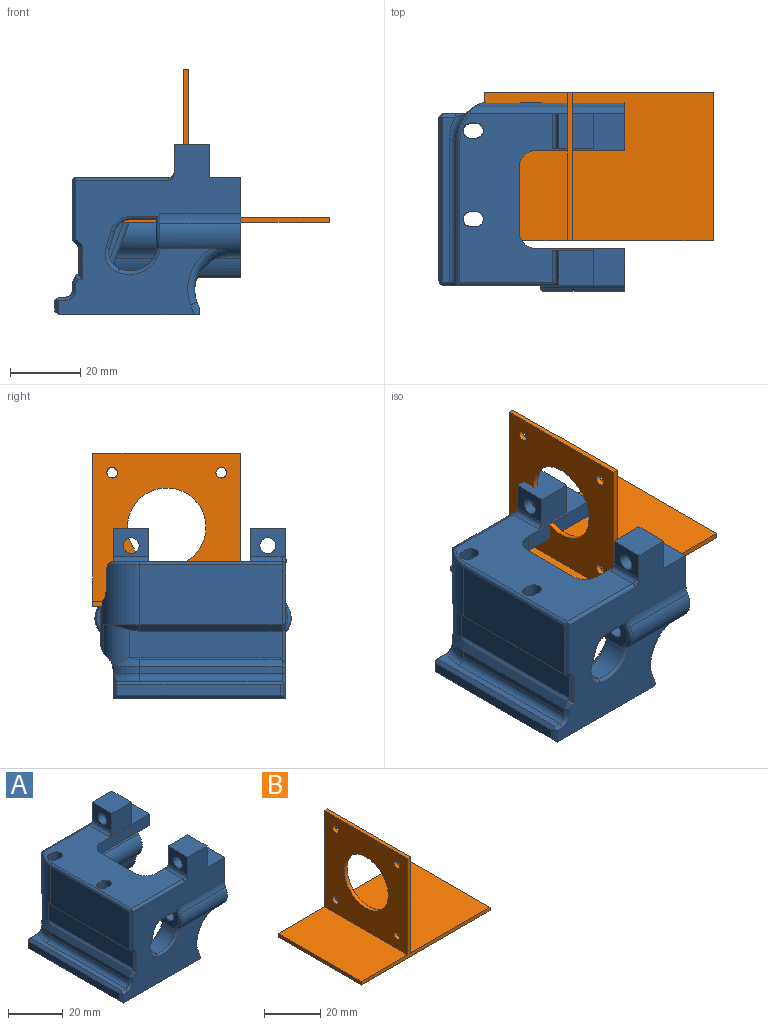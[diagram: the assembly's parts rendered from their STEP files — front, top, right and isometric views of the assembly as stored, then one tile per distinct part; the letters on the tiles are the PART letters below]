
ASSEMBLY  parts=2 mates=1
PART A: 215 faces, bbox 55x69.2x51.2 mm
  f0: cylinder r=11mm len=7.18mm, axis (0,0,-1), area 15.4mm2, adj f1,f133,f176,f195,f196
  f1: plane 40.6x2mm, normal (-1,0,0), area 81.2mm2, adj f0,f132,f175,f187
  f2: cylinder r=11mm len=25.09mm, axis (0,0,-1), area 262.1mm2, adj f47,f72,f73,f77,f80,f81,f174,f178
  f3: cylinder r=2mm len=25mm, axis (0,0,-1), area 11.6mm2, adj f7,f33,f36,f60,f137
  f4: plane 14x5.5mm, normal (1,0,0), area 77mm2, adj f5,f33,f60,f172
  f5: plane 22.15x7.04mm, normal (0.45,0,0.89), area 85.2mm2, adj f4,f7,f22,f26,f36,f60,f104,f124
  f6: plane 22.15x7.04mm, normal (0.45,0,-0.89), area 85.2mm2, adj f7,f9,f11,f22,f25,f26,f60,f126
  f7: plane 11x0.03mm, normal (-1,0,0), area 0.3mm2, adj f3,f5,f6,f149
  f8: plane 49x46.8mm, normal (0,0,1), area 1158.1mm2, adj f28,f50,f59,f60,f61,f62,f63,f64
  f9: plane 7x3.25mm, normal (1,0,0), area 22.7mm2, adj f6,f25,f34,f136
  f10: plane 7x3.25mm, normal (1,0,0), area 22.7mm2, adj f24,f49,f127,f134
  f11: plane 5x4.05mm, normal (1,0,0), area 20.2mm2, adj f6,f136,f170,f207
  f12: plane 7x0.55mm, normal (1,0,0), area 3.8mm2, adj f43,f45,f49,f127,f134
  f13: cylinder r=2mm len=2mm, axis (0,0,-1), area 6.3mm2, adj f15,f34,f52,f58
  f14: cylinder r=2mm len=2mm, axis (0,0,-1), area 6.3mm2, adj f15,f34,f51,f58
  f15: plane 2x0.2mm, normal (1,0,0), area 0.4mm2, adj f13,f14,f34,f58
  f16: cylinder r=2mm len=2mm, axis (0,0,-1), area 6.3mm2, adj f17,f49,f54,f58
  f17: plane 2x0.2mm, normal (1,0,0), area 0.4mm2, adj f16,f18,f49,f58
  f18: cylinder r=2mm len=2mm, axis (0,0,-1), area 6.3mm2, adj f17,f49,f56,f58
  f19: cylinder r=5mm len=3.66mm, axis (-1,0,0), area 7.5mm2, adj f20,f21,f71,f130,f131
  f20: cylinder r=5mm len=2.74mm, axis (-1,0,0), area 0.4mm2, adj f19,f21,f71,f131
  f21: cylinder r=9.6mm len=39.88mm, axis (1,0,0), area 186.7mm2, adj f19,f20,f66,f71,f88,f89,f129,f130
  f22: plane 27.41x10.4mm, normal (0,-1,0), area 123.5mm2, adj f5,f6,f25,f103,f104,f110,f124,f125
  f23: plane 27.41x10.4mm, normal (0,1,0), area 123.5mm2, adj f24,f101,f102,f106,f127,f128,f129,f130
  f24: cylinder r=3mm len=8.5mm, axis (0,0,1), area 36.2mm2, adj f10,f23,f49,f105,f127
  f25: cylinder r=3mm len=8.5mm, axis (0,0,-1), area 36.2mm2, adj f6,f9,f22,f34,f109
  f26: plane 41.8x31mm, normal (0,1,0), area 577.4mm2, adj f5,f6,f28,f30,f58,f124,f125,f126
  f27: plane 45.17x8.35mm, normal (0,0,-1), area 329.3mm2, adj f41,f42,f48,f55,f62,f63,f65,f66
  f28: plane 22.19x12.09mm, normal (1,0,0), area 202.2mm2, adj f8,f26,f29,f30,f50,f119,f120,f123
  f29: cylinder r=6.09mm len=23mm, axis (1,0,0), area 98.7mm2, adj f28,f120,f161,f168
  f30: cylinder r=6.09mm len=24mm, axis (1,0,0), area 314.6mm2, adj f26,f28,f31,f50,f120,f155,f160,f165
  f31: plane 10.19x9.28mm, normal (-1,0,0), area 64.3mm2, adj f30,f32,f115,f119,f156,f161,f165,f166
  f32: plane 7.11x6.5mm, normal (0,0,-1), area 46.2mm2, adj f31,f118,f156,f161
  f33: plane 17.17x14mm, normal (0,0,-1), area 191.8mm2, adj f3,f4,f36,f59,f60,f61,f67,f103
  f34: plane 19.69x6.7mm, normal (0,0,1), area 53.5mm2, adj f9,f13,f14,f15,f25,f35,f51,f52
  f35: plane 6.4x2mm, normal (1,0,0), area 12.8mm2, adj f34,f51,f58,f206
  f36: plane 14x4.67mm, normal (1,0,0), area 65.4mm2, adj f3,f5,f33,f104
  f37: plane 6.74x6.42mm, normal (0.92,0,-0.39), area 43.7mm2, adj f70,f79,f85,f86,f94,f95
  f38: plane 1x0.64mm, normal (0.92,0,-0.39), area 0.7mm2, adj f44,f45,f57,f99
  f39: cylinder r=6mm len=40.16mm, axis (1,0,0), area 408.5mm2, adj f65,f66,f75,f84,f88
  f40: cylinder r=6mm len=23.5mm, axis (1,0,0), area 201.7mm2, adj f66,f77,f90,f97
  f41: plane 6.67x1.68mm, normal (-1,0,0), area 0.5mm2, adj f27,f42,f74,f75,f84
  f42: plane 17.05x3.25mm, normal (0,-1,0), area 55.4mm2, adj f27,f41,f65,f84
  f43: cylinder r=5mm len=19.17mm, axis (-1,0,0), area 27.8mm2, adj f12,f45,f89,f99,f127
  f44: plane 15.23x7.83mm, normal (0,1,0), area 69.2mm2, adj f38,f57,f58,f82,f99,f191,f193,f194
  f45: plane 10.2x7.27mm, normal (0,-1,0), area 43mm2, adj f12,f38,f43,f49,f99
  f46: plane 5.72x4.3mm, normal (0,0,-1), area 24.6mm2, adj f70,f78,f83,f91
  f47: plane 40.6x17mm, normal (-1,0,0), area 690.2mm2, adj f2,f177,f179,f198
  f48: plane 14x4.67mm, normal (1,0,0), area 65.4mm2, adj f27,f55,f102,f128
  f49: plane 15.19x6.7mm, normal (0,0,1), area 45.6mm2, adj f10,f12,f16,f17,f18,f24,f45,f53
  f50: plane 52.4x49.1mm, normal (0,-1,0), area 1198.7mm2, adj f8,f28,f30,f58,f138,f140,f141,f155
  f51: plane 3x2mm, normal (0,1,0), area 6mm2, adj f14,f34,f35,f58
  f52: plane 3x2mm, normal (0,-1,0), area 6mm2, adj f13,f34,f53,f58
  f53: plane 20.8x2mm, normal (1,0,0), area 41.6mm2, adj f34,f49,f52,f54,f58,f100
  f54: plane 3x2mm, normal (0,1,0), area 6mm2, adj f16,f49,f53,f58
  f55: cylinder r=2mm len=25mm, axis (0,0,-1), area 11.6mm2, adj f27,f48,f63,f87,f135
  f56: plane 3x2mm, normal (0,-1,0), area 6mm2, adj f18,f49,f57,f58
  f57: plane 2.9x2mm, normal (1,0,0), area 5.8mm2, adj f38,f44,f49,f56,f58
  f58: plane 49.03x40.03mm, normal (0,0,-1), area 747.4mm2, adj f13,f14,f15,f16,f17,f18,f26,f35
  f59: plane 5x1.5mm, normal (0,1,0), area 7.5mm2, adj f8,f33,f60,f67
  f60: cylinder r=2.15mm len=30mm, axis (0,0,-1), area 150.4mm2, adj f3,f4,f5,f6,f8,f33,f59,f61
  f61: plane 5x1.5mm, normal (0,-1,0), area 7.5mm2, adj f8,f33,f60,f67
  f62: plane 5x1.5mm, normal (0,1,0), area 7.5mm2, adj f8,f27,f63,f65
  f63: cylinder r=2.15mm len=30mm, axis (0,0,-1), area 165.2mm2, adj f8,f27,f55,f62,f64,f127,f135
  f64: plane 29.5x1.5mm, normal (0,-1,0), area 43.7mm2, adj f8,f63,f65,f127
  f65: cylinder r=2.15mm len=28.75mm, axis (0,0,-1), area 128.2mm2, adj f8,f27,f39,f42,f62,f64,f79,f83
  f66: plane 28.45x15.72mm, normal (1,0,0), area 225.5mm2, adj f8,f21,f27,f39,f40,f72,f73,f74
  f67: cylinder r=2.15mm len=5mm, axis (0,0,-1), area 33.8mm2, adj f8,f33,f59,f61
  f68: plane 47x3.69mm, normal (0,0,1), area 97.5mm2, adj f132,f133,f184,f190,f193
  f69: plane 46.59x3mm, normal (-1,0,0), area 139.8mm2, adj f188,f189,f190,f191
  f70: cylinder r=2.9mm len=6.25mm, axis (0,1,0), area 20.7mm2, adj f37,f46,f79,f92,f93
  f71: plane 2.55x1.16mm, normal (0.92,0,-0.39), area 0.2mm2, adj f19,f20,f21
  f72: plane 42.51x5.47mm, normal (0,1,0), area 232.7mm2, adj f2,f66,f73,f77
  f73: cylinder r=2.5mm len=43.52mm, axis (1,0,0), area 147.7mm2, adj f2,f8,f66,f72,f142,f199
  f74: plane 24x2.98mm, normal (0,-1,0), area 71.5mm2, adj f27,f41,f66,f75
  f75: cylinder r=5mm len=24mm, axis (1,0,0), area 99.7mm2, adj f39,f41,f66,f74
  f76: cylinder r=2.25mm len=24mm, axis (1,0,0), area 339.3mm2, adj f66,f78
  f77: cylinder r=6mm len=42.51mm, axis (1,0,0), area 179.7mm2, adj f2,f40,f66,f72,f80,f91,f92,f96
  f78: plane 9.67x8.43mm, normal (-1,0,0), area 53mm2, adj f46,f76,f83,f85,f86,f91,f95,f96
  f79: plane 12.75x7.58mm, normal (0,-1,0), area 70.6mm2, adj f37,f65,f70,f83,f85
  f80: plane 36.85x11.25mm, normal (0,1,0), area 128.2mm2, adj f2,f66,f77,f81,f92,f93,f94,f95
  f81: cylinder r=5mm len=43.61mm, axis (-1,0,0), area 165.8mm2, adj f2,f66,f80,f82,f174,f196
  f82: cylinder r=6mm len=44.48mm, axis (-1,0,0), area 91.8mm2, adj f44,f66,f81,f89,f99,f196
  f83: cylinder r=5.5mm len=17.05mm, axis (1,0,0), area 28.9mm2, adj f46,f65,f78,f79,f85
  f84: cylinder r=4.32mm len=17.05mm, axis (1,0,0), area 65.5mm2, adj f39,f41,f42,f65
  f85: cylinder r=4.2mm len=17.05mm, axis (1,0,0), area 141.1mm2, adj f37,f65,f78,f79,f83,f86
  f86: plane 9.75x3.7mm, normal (0,-0.03,1), area 36mm2, adj f37,f78,f85,f95
  f87: plane 11x0.03mm, normal (-1,0,0), area 0.3mm2, adj f55,f127,f128,f153
  f88: cylinder r=3.72mm len=40.3mm, axis (1,0,0), area 104.5mm2, adj f21,f39,f65,f66,f128,f129
  f89: cylinder r=1.71mm len=40.09mm, axis (1,0,0), area 96.6mm2, adj f21,f43,f66,f82,f99,f127,f131
  f90: plane 23.5x0.8mm, normal (0,0.94,-0.33), area 20mm2, adj f40,f66,f95,f98
  f91: cylinder r=0.5mm len=4.8mm, axis (1,0,0), area 4.8mm2, adj f46,f77,f78,f92,f96
  f92: bspline ~3.08x1.66mm, area 2.2mm2, adj f70,f77,f80,f91,f93
  f93: torus R=3.4mm, axis (0,1,0), area 1.3mm2, adj f70,f80,f92,f94
  f94: cylinder r=0.5mm len=7.34mm, axis (-0.39,0,-0.92), area 5.8mm2, adj f37,f80,f93,f95
  f95: cylinder r=0.5mm len=34.45mm, axis (-1,0,0), area 9.1mm2, adj f37,f66,f78,f80,f86,f90,f94,f98
  f96: cone r=6.5mm half-angle=45deg, axis (-1,0,0), area 0.5mm2, adj f77,f78,f91,f97
  f97: cone r=6mm half-angle=45deg, axis (1,0,0), area 5.8mm2, adj f40,f78,f96,f98
  f98: plane 1.05x0.66mm, normal (-0.71,0.67,-0.24), area 0.5mm2, adj f78,f90,f95,f97
  f99: bspline ~24.29x14.9mm, area 23.7mm2, adj f38,f43,f44,f45,f82,f89
  f100: plane 28.47x10.8mm, normal (0.93,0,-0.35), area 91.4mm2, adj f53,f105,f106,f107,f109,f110,f111,f122
  f101: cylinder r=3mm len=16.8mm, axis (-1,0,0), area 65.9mm2, adj f23,f27,f102,f107,f108,f201
  f102: cylinder r=3mm len=15.5mm, axis (0,0,1), area 62.4mm2, adj f23,f48,f101,f128
  f103: cylinder r=3mm len=14.8mm, axis (1,0,0), area 63.3mm2, adj f22,f33,f104,f111,f112,f122
  f104: cylinder r=3mm len=15.5mm, axis (0,0,-1), area 62.4mm2, adj f5,f22,f36,f103
  f105: bspline ~6.16x3.09mm, area 3.1mm2, adj f24,f49,f100,f106
  f106: cylinder r=1.5mm len=27.94mm, axis (0.35,0,0.93), area 69.1mm2, adj f23,f100,f105,f107
  f107: bspline ~1.77x1.54mm, area 0.8mm2, adj f100,f101,f106,f108,f122,f201
  f108: bspline ~3.03x2.61mm, area 1.5mm2, adj f101,f107,f201
  f109: bspline ~6.16x3.09mm, area 3.1mm2, adj f25,f34,f100,f110
  f110: cylinder r=1.5mm len=27.94mm, axis (-0.35,0,-0.93), area 69.1mm2, adj f22,f100,f109,f111
  f111: bspline ~1.6x1.52mm, area 0.8mm2, adj f100,f103,f110,f112,f122
  f112: bspline ~3.03x2.61mm, area 1.2mm2, adj f103,f111,f122
  f113: plane 8.44x2.89mm, normal (1,0,0), area 13.2mm2, adj f58,f114,f212,f214
  f114: plane 4.5x1.48mm, normal (0.94,0,0.35), area 6.4mm2, adj f113,f210,f212,f214
  f115: cylinder r=7.86mm len=10.6mm, axis (0,-1,0), area 86mm2, adj f31,f116,f160,f165,f167
  f116: cylinder r=4.82mm len=6.5mm, axis (0,-1,0), area 46.5mm2, adj f115,f117,f159,f164
  f117: plane 6.5x4.63mm, normal (0.96,0,-0.29), area 31.4mm2, adj f116,f118,f158,f163
  f118: cylinder r=5mm len=6.5mm, axis (0,-1,0), area 41.5mm2, adj f32,f117,f157,f162
  f119: cylinder r=2.25mm len=24mm, axis (1,0,0), area 339.3mm2, adj f28,f31
  f120: plane 23x2.06mm, normal (0,1,0), area 47.4mm2, adj f28,f29,f30,f169
  f121: plane 25x5mm, normal (0,-1,0), area 125mm2, adj f8,f27,f66,f201
  f122: plane 18.21x8.74mm, normal (1,0,0), area 108.6mm2, adj f8,f33,f100,f103,f107,f111,f112,f201
  f123: plane 25x5.17mm, normal (0,1,0), area 129.3mm2, adj f8,f28,f171,f202
  f124: cylinder r=2mm len=20mm, axis (0,1,0), area 44.3mm2, adj f5,f22,f26,f125
  f125: plane 20x2.53mm, normal (1,0,0), area 50.6mm2, adj f22,f26,f124,f126
  f126: cylinder r=2mm len=20mm, axis (0,1,0), area 44.3mm2, adj f6,f22,f26,f125
  f127: plane 14.13x5.53mm, normal (0.45,0,-0.89), area 50.5mm2, adj f10,f12,f23,f24,f43,f63,f64,f65
  f128: plane 11.3x5.68mm, normal (0.45,0,0.89), area 40.7mm2, adj f23,f48,f65,f87,f88,f102,f129,f153
  f129: cylinder r=2mm len=11.12mm, axis (0,1,0), area 24mm2, adj f21,f23,f88,f128,f130
  f130: plane 11.71x2.53mm, normal (1,0,0), area 28.8mm2, adj f19,f21,f23,f129,f131
  f131: cylinder r=2mm len=12.81mm, axis (0,1,0), area 27.2mm2, adj f19,f20,f21,f23,f89,f127,f130
  f132: cylinder r=2mm len=40.6mm, axis (0,-1,0), area 127.5mm2, adj f1,f68,f133,f186
  f133: torus R=13mm, axis (0,0,-1), area 22.2mm2, adj f0,f68,f132,f194
  f134: cylinder r=3.5mm len=7mm, axis (0,0,-1), area 62.8mm2, adj f10,f12,f49,f135
  f135: plane 6.71x2.5mm, normal (0,0,-1), area 9.2mm2, adj f55,f63,f127,f134
  f136: cylinder r=3.5mm len=7mm, axis (0,0,-1), area 64.8mm2, adj f9,f11,f34,f137,f207
  f137: plane 6.71x2.5mm, normal (0,0,-1), area 9.2mm2, adj f3,f6,f60,f136
  f138: plane 10x9.5mm, normal (1,0,0), area 79.1mm2, adj f8,f50,f139,f141,f148
  f139: plane 11.5x9.5mm, normal (0,1,0), area 95.5mm2, adj f8,f138,f140,f141,f203
  f140: plane 10x8.21mm, normal (-1,0,0), area 64.2mm2, adj f50,f139,f141,f148,f203,f204
  f141: plane 10x10mm, normal (0,0,1), area 100mm2, adj f50,f138,f139,f140
  f142: plane 11.5x9.5mm, normal (0,1,0), area 95.5mm2, adj f73,f143,f145,f146,f205
  f143: plane 10x8mm, normal (-1,0,0), area 64.1mm2, adj f142,f144,f146,f147,f205
  f144: plane 11.5x9.5mm, normal (0,-1,0), area 95.5mm2, adj f8,f143,f145,f146,f205
  f145: plane 10x9.5mm, normal (1,0,0), area 79.1mm2, adj f8,f142,f144,f146,f147
  f146: plane 10x10mm, normal (0,0,1), area 100mm2, adj f142,f143,f144,f145
  f147: cylinder r=2.25mm len=10mm, axis (-1,0,0), area 141.4mm2, adj f143,f145
  f148: cylinder r=2.25mm len=10mm, axis (-1,0,0), area 141.4mm2, adj f138,f140
  f149: cylinder r=2.15mm len=11mm, axis (0,0,1), area 10.9mm2, adj f5,f6,f7,f152
  f150: plane 10x1.5mm, normal (0,1,0), area 13.9mm2, adj f5,f6,f60,f151
  f151: cylinder r=2.15mm len=8.5mm, axis (0,0,1), area 57.4mm2, adj f5,f6,f150,f152
  f152: plane 10x1.5mm, normal (0,-1,0), area 13.9mm2, adj f5,f6,f149,f151
  f153: cylinder r=2.15mm len=11mm, axis (0,0,1), area 10.9mm2, adj f87,f127,f128,f154
  f154: plane 10x1.5mm, normal (0,1,0), area 13.9mm2, adj f65,f127,f128,f153
  f155: cylinder r=5mm len=23mm, axis (1,0,0), area 62.3mm2, adj f28,f30,f50,f166
  f156: cylinder r=1mm len=7.84mm, axis (-1,0,0), area 11.5mm2, adj f31,f32,f50,f157,f166
  f157: torus R=6mm, axis (0,1,0), area 10.7mm2, adj f50,f118,f156,f158
  f158: cylinder r=1mm len=4.92mm, axis (-0.29,0,-0.96), area 7.6mm2, adj f50,f117,f157,f159
  f159: torus R=5.82mm, axis (0,1,0), area 12.1mm2, adj f50,f116,f158,f160
  f160: torus R=8.86mm, axis (0,1,0), area 22.8mm2, adj f30,f50,f115,f159,f167
  f161: cylinder r=1mm len=31.11mm, axis (-1,0,0), area 22mm2, adj f26,f28,f29,f31,f32,f162,f168
  f162: torus R=6mm, axis (0,-1,0), area 10.7mm2, adj f26,f118,f161,f163
  f163: cylinder r=1mm len=4.92mm, axis (-0.29,0,-0.96), area 7.6mm2, adj f26,f117,f162,f164
  f164: torus R=5.82mm, axis (0,-1,0), area 12.1mm2, adj f26,f116,f163,f165
  f165: torus R=8.86mm, axis (0,-1,0), area 21.7mm2, adj f26,f30,f31,f115,f164
  f166: torus R=6mm, axis (1,0,0), area 2.9mm2, adj f31,f50,f155,f156,f167
  f167: torus R=5.09mm, axis (1,0,0), area 12.8mm2, adj f30,f31,f115,f160,f166
  f168: torus R=5.09mm, axis (1,0,0), area 6.3mm2, adj f29,f31,f161,f169
  f169: cylinder r=1mm len=4.5mm, axis (0,0,-1), area 5.1mm2, adj f30,f31,f120,f168
  f170: cylinder r=3mm len=6.5mm, axis (0,0,1), area 27.1mm2, adj f6,f11,f26,f209
  f171: cylinder r=3mm len=44.8mm, axis (-1,0,0), area 177mm2, adj f26,f28,f33,f123,f172,f202
  f172: cylinder r=3mm len=15.5mm, axis (0,0,1), area 62.4mm2, adj f4,f5,f26,f171
  f173: plane 43.64x8.09mm, normal (-1,0,0), area 321.1mm2, adj f174,f176,f177,f178,f181,f200
  f174: cylinder r=8mm len=11.45mm, axis (0,0,-1), area 85.1mm2, adj f2,f81,f173,f176,f178,f196
  f175: plane 40.6x2mm, normal (-0.89,0,0.45), area 90.8mm2, adj f1,f176,f185,f200
  f176: cone r=11mm half-angle=26.6deg, axis (0,0,-1), area 16.6mm2, adj f0,f173,f174,f175,f196,f200
  f177: plane 40.6x1.8mm, normal (-0.71,0,-0.71), area 103.3mm2, adj f47,f173,f178,f180
  f178: cone r=6mm half-angle=45deg, axis (0,0,1), area 15.7mm2, adj f2,f173,f174,f177
  f179: plane 18.1x1.23mm, normal (-0.71,-0.71,0), area 24.6mm2, adj f47,f50,f180,f197,f198
  f180: plane 2.8x2.21mm, normal (-0.5,-0.71,-0.5), area 3.6mm2, adj f50,f177,f179,f181
  f181: plane 9.61x1.4mm, normal (-0.71,-0.71,0), area 12.8mm2, adj f50,f173,f180,f183,f200
  f182: plane 4.5x0.71mm, normal (-0.71,-0.71,0), area 3.9mm2, adj f50,f184,f188,f189,f190
  f183: plane 1.8x1.4mm, normal (0,-0.71,0.71), area 1.6mm2, adj f50,f181,f185,f200
  f184: plane 2.5x1mm, normal (0,-0.71,0.71), area 3.2mm2, adj f50,f68,f182,f186,f190
  f185: plane 2.24x1.62mm, normal (-0.63,-0.71,0.32), area 2.6mm2, adj f50,f175,f183,f187
  f186: cone r=3mm half-angle=45deg, axis (0,-1,0), area 5.6mm2, adj f50,f132,f184,f187
  f187: plane 2x1mm, normal (-0.71,-0.71,0), area 2.7mm2, adj f1,f50,f185,f186
  f188: plane 3.59x0.71mm, normal (-0.92,-0.38,0), area 2.5mm2, adj f69,f182,f189,f190
  f189: plane 49x1mm, normal (-0.71,0,-0.71), area 67.8mm2, adj f58,f69,f182,f188,f191
  f190: plane 47.5x1mm, normal (-0.71,0,0.71), area 66.7mm2, adj f68,f69,f182,f184,f188,f192
  f191: plane 4x1mm, normal (-0.71,0.71,0), area 4.9mm2, adj f44,f69,f189,f192
  f192: plane 1x1mm, normal (-0.58,0.58,0.58), area 0.9mm2, adj f190,f191,f193
  f193: plane 3.69x1mm, normal (0,0.71,0.71), area 5.2mm2, adj f44,f68,f192,f194
  f194: bspline ~3.64x3mm, area 5mm2, adj f44,f133,f193,f195
  f195: plane 0.77x0.66mm, normal (-0.42,0.91,0), area 0.6mm2, adj f0,f44,f194,f196
  f196: bspline ~5.18x3.5mm, area 2.7mm2, adj f0,f81,f82,f174,f176,f195
  f197: cylinder r=1mm len=26.9mm, axis (-1,0,0), area 41.9mm2, adj f8,f50,f179,f198,f204
  f198: cylinder r=1mm len=41.1mm, axis (0,1,0), area 64.2mm2, adj f8,f47,f179,f197,f199
  f199: torus R=10mm, axis (0,0,1), area 14.6mm2, adj f2,f8,f73,f198
  f200: plane 43.34x0.8mm, normal (-0.71,0,0.71), area 47.8mm2, adj f173,f175,f176,f181,f183
  f201: cylinder r=5mm len=8.29mm, axis (0,0,-1), area 43.9mm2, adj f8,f27,f101,f107,f108,f121,f122
  f202: cylinder r=5mm len=5.17mm, axis (0,0,1), area 39.5mm2, adj f8,f33,f122,f123,f171
  f203: cylinder r=1.5mm len=9mm, axis (0,-1,0), area 21.2mm2, adj f8,f139,f140,f204
  f204: torus R=2.5mm, axis (-1,0,0), area 3.3mm2, adj f50,f140,f197,f203
  f205: cylinder r=1.5mm len=10mm, axis (0,-1,0), area 23.6mm2, adj f8,f142,f143,f144
  f206: cylinder r=2mm len=4mm, axis (0,0,-1), area 9.4mm2, adj f26,f35,f58,f208
  f207: cylinder r=2mm len=4.05mm, axis (0,-1,0), area 12.7mm2, adj f11,f34,f136,f209
  f208: cylinder r=2mm len=3mm, axis (1,0,0), area 6.3mm2, adj f26,f34,f206,f209
  f209: torus R=1mm, axis (0,0,1), area 11.2mm2, adj f34,f170,f207,f208
  f210: bspline ~20.05x15.16mm, area 117.5mm2, adj f30,f114,f211,f213
  f211: bspline ~17.89x12.48mm, area 47.8mm2, adj f26,f30,f210,f212
  f212: cylinder r=2mm len=3.87mm, axis (0.35,0,-0.94), area 8.6mm2, adj f26,f58,f113,f114,f211
  f213: bspline ~18.15x11.4mm, area 45.8mm2, adj f30,f50,f210,f214
  f214: cylinder r=2mm len=3.94mm, axis (0.35,0,-0.94), area 8.9mm2, adj f50,f58,f113,f114,f213
PART B: 15 faces, bbox 65x42x43.5 mm
  f0: plane 42x40mm, normal (0,0,1), area 1680mm2, adj f1,f3,f4,f14
  f1: plane 65x43.5mm, normal (0,1,0), area 160.5mm2, adj f0,f2,f4,f5,f6,f7,f13,f14
  f2: plane 42x1.5mm, normal (-1,0,0), area 63mm2, adj f1,f3,f5,f6
  f3: plane 65x43.5mm, normal (0,-1,0), area 160.5mm2, adj f0,f2,f4,f5,f6,f7,f13,f14
  f4: plane 42x1.5mm, normal (1,0,0), area 63mm2, adj f0,f1,f3,f5
  f5: plane 65x42mm, normal (0,0,-1), area 2730mm2, adj f1,f2,f3,f4
  f6: plane 42x23.5mm, normal (0,0,1), area 987mm2, adj f1,f2,f3,f13
  f7: plane 42x1.5mm, normal (0,0,1), area 63mm2, adj f1,f3,f13,f14
  f8: cylinder r=11.15mm len=22.3mm, axis (1,0,0), area 105.1mm2, adj f13,f14
  f9: cylinder r=1.5mm len=3mm, axis (1,0,0), area 14.1mm2, adj f13,f14
  f10: cylinder r=1.5mm len=3mm, axis (1,0,0), area 14.1mm2, adj f13,f14
  f11: cylinder r=1.5mm len=3mm, axis (1,0,0), area 14.1mm2, adj f13,f14
  f12: cylinder r=1.5mm len=3mm, axis (1,0,0), area 14.1mm2, adj f13,f14
  f13: plane 42x42mm, normal (-1,0,0), area 1345.2mm2, adj f1,f3,f6,f7,f8,f9,f10,f11
  f14: plane 42x42mm, normal (1,0,0), area 1345.2mm2, adj f0,f1,f3,f7,f8,f9,f10,f11
PLACE A t=(17.67,1.87,3.25)mm
PLACE B t=(26.65,9.16,30.97)mm
MATE parallel A.f8 <-> B.f5  axis (0,0,1) through (11.28,-4.99,42.25)mm
